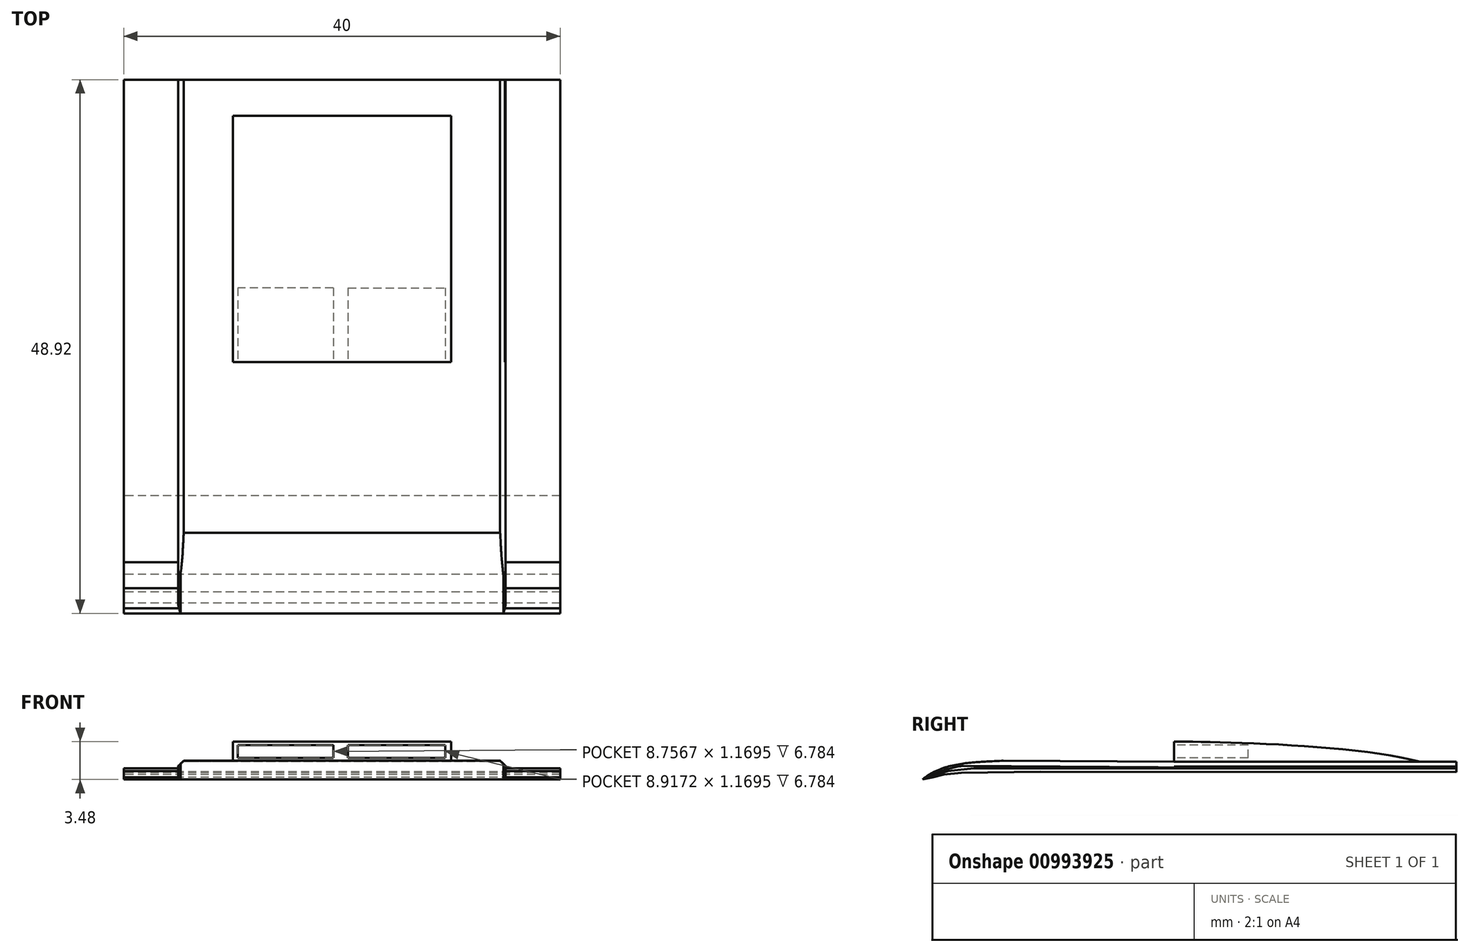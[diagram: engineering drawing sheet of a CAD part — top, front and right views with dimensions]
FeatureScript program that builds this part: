
annotation { "Feature Type Name" : "Feature", "Feature Type Description" : "" }
export const myFeature = defineFeature(function(context is Context, id is Id, definition is map)
    precondition{}
    {
        {
            var Q0;
            Q0=qCreatedBy(makeId("Right.planeOp"),FACE);
            var sketch = newSketch(context, id + "F0", { "sketchPlane" : qUnion([Q0])});
            skLineSegment(sketch, "E0", {"start": v(31.08, 2) * mm, "end": v(27.78, 2) * mm});
            skFitSpline(sketch, "E1", {"points": [v(27.78, 2) * mm, v(5.22, 3.87) * mm], "startDerivative": vector(-18.32, 5.03) * mm, "endDerivative": vector(-9.39, 0.02) * mm});
            skLineSegment(sketch, "E2", {"start": v(5.22, 2) * mm, "end": v(-10.45, 2.11) * mm});
            skFitSpline(sketch, "E3", {"points": [v(-10.45, 2.11) * mm, v(-17.84, 0.4) * mm], "startDerivative": vector(-8.63, -0.44) * mm, "endDerivative": vector(-5.73, -4.77) * mm});
            skLineSegment(sketch, "E4", {"start": v(-17.84, 0.4) * mm, "end": v(-17.37, 0.6) * mm});
            skLineSegment(sketch, "E5", {"start": v(5.22, 2) * mm, "end": v(5.22, 3.87) * mm});
            skLineSegment(sketch, "E6", {"start": v(-7.05, 1.1) * mm, "end": v(31.08, 1.06) * mm});
            skLineSegment(sketch, "E7", {"start": v(31.08, 1.06) * mm, "end": v(31.08, 2) * mm});
            skLineSegment(sketch, "E8", {"start": v(5.22, 2) * mm, "end": v(27.78, 2) * mm});
            skLineSegment(sketch, "E9", {"start": v(-17.37, 0.6) * mm, "end": v(-15.53, 1.17) * mm});
            skLineSegment(sketch, "E10", {"start": v(-15.53, 1.17) * mm, "end": v(-13.14, 1.41) * mm});
            skLineSegment(sketch, "E11", {"start": v(-13.14, 1.41) * mm, "end": v(-7.15, 1.41) * mm});
            skLineSegment(sketch, "E12", {"start": v(-7.15, 1.41) * mm, "end": v(31.08, 1.38) * mm});
            skLineSegment(sketch, "E13", {"start": v(-17.84, 0.4) * mm, "end": v(-16.9, 0.6) * mm});
            skLineSegment(sketch, "E14", {"start": v(-16.9, 0.6) * mm, "end": v(-15.9, 0.85) * mm});
            skLineSegment(sketch, "E15", {"start": v(-15.9, 0.85) * mm, "end": v(-14.27, 1) * mm});
            skLineSegment(sketch, "E16", {"start": v(-14.27, 1) * mm, "end": v(-7.05, 1.1) * mm});
            skSolve(sketch);
        }
        {
            var Q0;
            Q0=makeQuery(id+"F0.imprint","IMPRINT",FACE,{"disambiguationData":[TD([[makeQuery(id+"F0.imprint","IMPRINT",EDGE,{"derivedFrom":sQuery(id+"F0.wireOp",EDGE,"E0")}),1.0]])]});
            extrude(context, id + "F1", {"entities" : qUnion([Q0]), "endBound" : BoundingType.SYMMETRIC, "depth" : 30 * mm, "offsetDistance" : 25 * mm});
        }
        {
            var Q0;
            Q0=makeQuery(id+"F0.imprint","IMPRINT",FACE,{"disambiguationData":[TD([[makeQuery(id+"F0.imprint","IMPRINT",EDGE,{"derivedFrom":sQuery(id+"F0.wireOp",EDGE,"E1")}),1.0]])]});
            extrude(context, id + "F2", {"entities" : qUnion([Q0]), "operationType" : NewBodyOperationType.ADD, "endBound" : BoundingType.SYMMETRIC, "depth" : 20 * mm, "offsetDistance" : 25 * mm});
        }
        {
            var Q0;
            Q0=qCreatedBy(makeId("Front.planeOp"),FACE);
            var sketch = newSketch(context, id + "F3", { "sketchPlane" : qUnion([Q0])});
            skLineSegment(sketch, "E17", {"start": v(0, 0) * mm, "end": v(0, 3.87) * mm});
            skLineSegment(sketch, "E18", {"start": v(0, 3.54) * mm, "end": v(9.48, 3.54) * mm});
            skLineSegment(sketch, "E19", {"start": v(9.48, 3.54) * mm, "end": v(9.48, 2.37) * mm});
            skLineSegment(sketch, "E20", {"start": v(9.48, 2.37) * mm, "end": v(-9.55, 2.37) * mm});
            skLineSegment(sketch, "E21", {"start": v(-9.55, 2.37) * mm, "end": v(-9.55, 3.54) * mm});
            skLineSegment(sketch, "E22", {"start": v(-9.55, 3.54) * mm, "end": v(0, 3.54) * mm});
            skLineSegment(sketch, "E23", {"start": v(0.56, 3.54) * mm, "end": v(0.56, 2.37) * mm});
            skLineSegment(sketch, "E24", {"start": v(-0.8, 2.37) * mm, "end": v(-0.8, 3.54) * mm});
            skSolve(sketch);
        }
        {
            var Q0;
            {var subQ0=sQuery(id+"F3.wireOp",EDGE,"E19");Q0=makeQuery(id+"F3.imprint","IMPRINT",FACE,{"disambiguationData":[TD([[makeQuery(id+"F3.imprint","IMPRINT",EDGE,{"derivedFrom":subQ0}),-1.0]])]});}
            var Q1;
            {var subQ0=sQuery(id+"F3.wireOp",EDGE,"E21");Q1=makeQuery(id+"F3.imprint","IMPRINT",FACE,{"disambiguationData":[TD([[makeQuery(id+"F3.imprint","IMPRINT",EDGE,{"derivedFrom":subQ0}),-1.0]])]});}
            extrude(context, id + "F4", {"entities" : qUnion([Q0, Q1]), "operationType" : NewBodyOperationType.REMOVE, "oppositeDirection" : true, "depth" : 12 * mm, "offsetDistance" : 25 * mm});
        }
        {
            var Q0;
            {var subQ1=sQuery(id+"F0.wireOp",EDGE,"E6");Q0=makeQuery(id+"F0.imprint","IMPRINT",FACE,{"disambiguationData":[TD([[makeQuery(id+"F0.imprint","IMPRINT",EDGE,{"derivedFrom":subQ1}),1.0]])]});}
            extrude(context, id + "F5", {"entities" : qUnion([Q0]), "operationType" : NewBodyOperationType.ADD, "endBound" : BoundingType.SYMMETRIC, "depth" : 40 * mm, "offsetDistance" : 25 * mm});
        }
        {
            var Q0;
            Q0=makeQuery(id+"F1.opExtrude","CAP_EDGE",EDGE,{"disambiguationData":[OSD([sQuery(id+"F0.wireOp",EDGE,"E0"),sQuery(id+"F0.wireOp",EDGE,"E2"),sQuery(id+"F0.wireOp",EDGE,"E8")])],"isStart":false});
            var Q1;
            Q1=makeQuery(id+"F1.opExtrude","CAP_EDGE",EDGE,{"disambiguationData":[OSD([sQuery(id+"F0.wireOp",EDGE,"E0"),sQuery(id+"F0.wireOp",EDGE,"E2"),sQuery(id+"F0.wireOp",EDGE,"E8")])],"isStart":true});
            var Q2;
            Q2=makeQuery(id+"F1.opExtrude","CAP_EDGE",EDGE,{"disambiguationData":[OSD([sQuery(id+"F0.wireOp",EDGE,"E2")])],"isStart":false});
            chamfer(context, id + "F6", {"entities" : qUnion([Q0, Q1, Q2]), "width" : 0.5 * mm, "tangentPropagation" : true});
        }
        {
            var Q0;
            Q0=makeQuery(id+"F1.opExtrude","CAP_EDGE",EDGE,{"disambiguationData":[OSD([sQuery(id+"F0.wireOp",EDGE,"E3")])],"isStart":false});
            var Q1;
            {var subQ0=sQuery(id+"F0.wireOp",EDGE,"E8");var subQ1=sQuery(id+"F0.wireOp",EDGE,"E2");var subQ2=sQuery(id+"F0.wireOp",EDGE,"E0");Q1=makeQuery(id+"F6.opChamfer","BLEND_EDGE",EDGE,{"blendedFrom":[makeQuery(id+"F1.opExtrude","CAP_EDGE",EDGE,{"disambiguationData":[OSD([subQ2,subQ1,subQ0])],"isStart":false}),makeQuery(id+"F1.opExtrude","CAP_FACE",FACE,{"disambiguationData":[OSD([subQ2,subQ1,sQuery(id+"F0.wireOp",EDGE,"E3"),sQuery(id+"F0.wireOp",EDGE,"E4"),sQuery(id+"F0.wireOp",EDGE,"E7"),subQ0,sQuery(id+"F0.wireOp",EDGE,"E9"),sQuery(id+"F0.wireOp",EDGE,"E10"),sQuery(id+"F0.wireOp",EDGE,"E11"),sQuery(id+"F0.wireOp",EDGE,"E12")])],"isStart":false})],"blendedInto":[makeQuery(id+"F1.opExtrude","CAP_FACE",FACE,{"disambiguationData":[OSD([subQ2,subQ1,sQuery(id+"F0.wireOp",EDGE,"E3"),sQuery(id+"F0.wireOp",EDGE,"E4"),sQuery(id+"F0.wireOp",EDGE,"E7"),subQ0,sQuery(id+"F0.wireOp",EDGE,"E9"),sQuery(id+"F0.wireOp",EDGE,"E10"),sQuery(id+"F0.wireOp",EDGE,"E11"),sQuery(id+"F0.wireOp",EDGE,"E12")])],"isStart":false})]});}
            var Q2;
            Q2=makeQuery(id+"F1.opExtrude","CAP_EDGE",EDGE,{"disambiguationData":[OSD([sQuery(id+"F0.wireOp",EDGE,"E3")])],"isStart":true});
            chamfer(context, id + "F7", {"entities" : qUnion([Q0, Q1, Q2]), "width" : 0.2 * mm, "tangentPropagation" : true});
        }
    });
